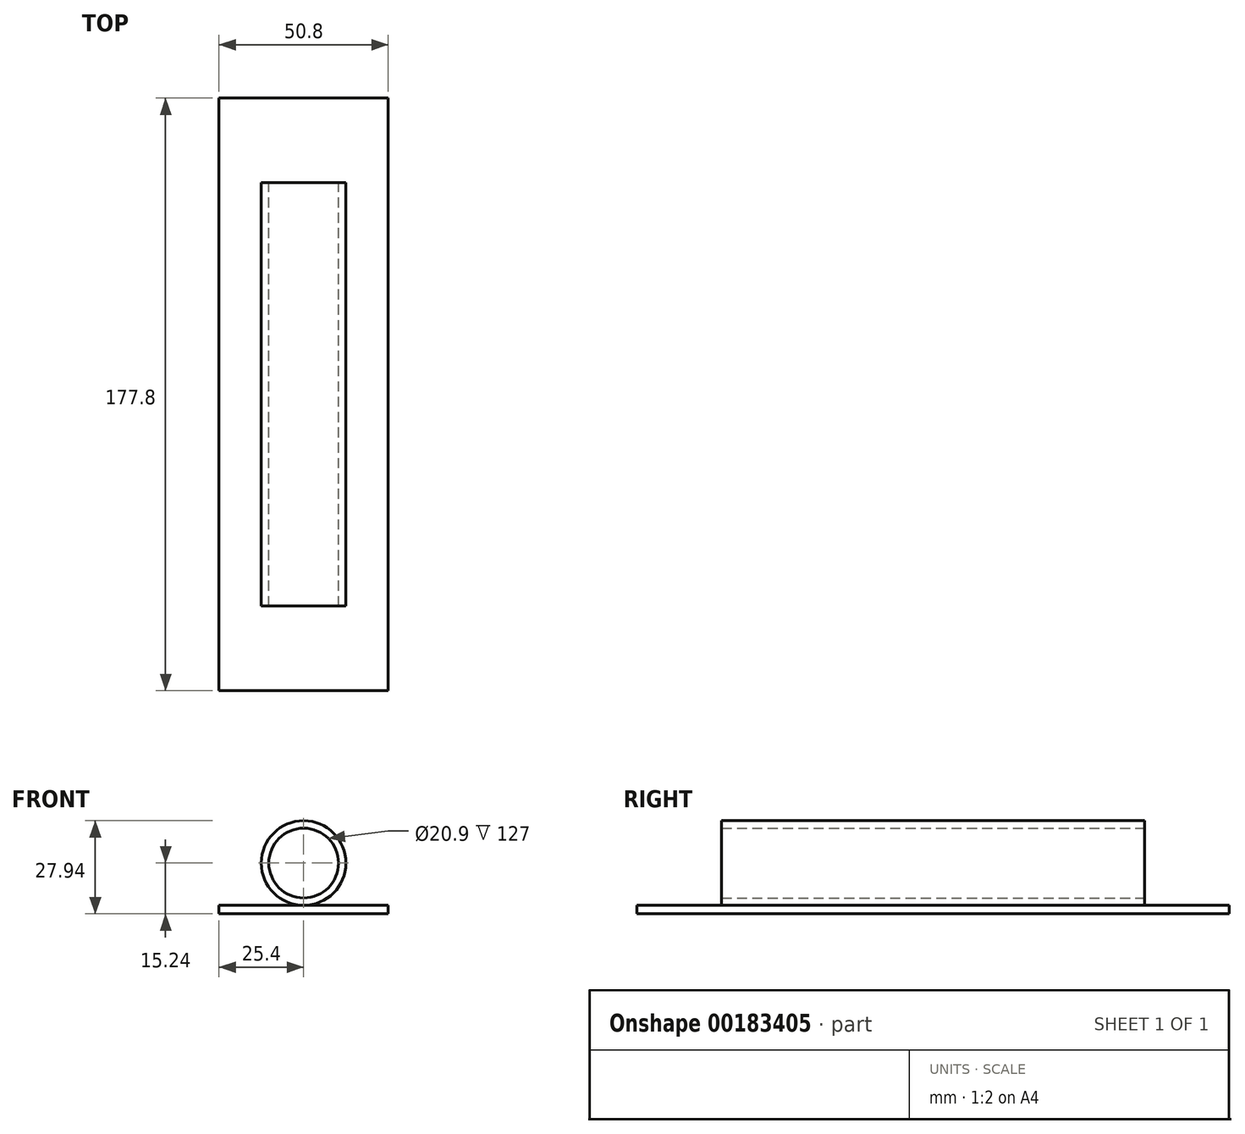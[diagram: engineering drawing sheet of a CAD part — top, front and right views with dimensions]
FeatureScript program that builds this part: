
annotation { "Feature Type Name" : "Feature", "Feature Type Description" : "" }
export const myFeature = defineFeature(function(context is Context, id is Id, definition is map)
    precondition{}
    {
        {
            var Q0;
            Q0=qCreatedBy(makeId("Front.planeOp"),FACE);
            var sketch = newSketch(context, id + "F0", { "sketchPlane" : qUnion([Q0])});
            skCircle(sketch, "E0", {"center": v(0, 0) * mm, "radius": 12.7 * mm});
            skCircle(sketch, "E1", {"center": v(0, 0) * mm, "radius": 10.45 * mm});
            skSolve(sketch);
        }
        {
            var Q0;
            Q0=makeQuery(id+"F0.imprint","IMPRINT",FACE,{"disambiguationData":[TD([[makeQuery(id+"F0.imprint","IMPRINT",EDGE,{"derivedFrom":sQuery(id+"F0.wireOp",EDGE,"E0")}),1.0]])]});
            var Q1;
            Q1=sQuery(id+"F0.wireOp",EDGE,"E0");
            var Q2;
            Q2=sQuery(id+"F0.wireOp",EDGE,"E1");
            extrude(context, id + "F1", {"entities" : qUnion([Q0]), "surfaceEntities" : qUnion([Q1, Q2]), "depth" : 127 * mm});
        }
        {
            var Q0;
            Q0=makeQuery(id+"F1.opExtrude","SWEPT_BODY",BODY,{"disambiguationData":[OSD([sQuery(id+"F0.wireOp",EDGE,"E0")])]});
            transform(context, id + "F2", {"entities" : qUnion([Q0]), "transformType" : TransformType.TRANSLATION_3D, "dx" : 0 * mm, "dy" : 0 * mm, "dz" : 12.7 * mm, "makeCopy" : false});
        }
        {
            var Q0;
            Q0=qCreatedBy(makeId("Top.planeOp"),FACE);
            var sketch = newSketch(context, id + "F3", { "sketchPlane" : qUnion([Q0])});
            skLineSegment(sketch, "E2.bottom", {"start": v(-25.4, 25.4) * mm, "end": v(25.4, 25.4) * mm});
            skLineSegment(sketch, "E2.top", {"start": v(-25.4, -152.4) * mm, "end": v(25.4, -152.4) * mm});
            skLineSegment(sketch, "E2.left", {"start": v(-25.4, 25.4) * mm, "end": v(-25.4, -152.4) * mm});
            skLineSegment(sketch, "E2.right", {"start": v(25.4, 25.4) * mm, "end": v(25.4, -152.4) * mm});
            skSolve(sketch);
        }
        {
            var Q0;
            Q0 = qSketchRegion(id + "F3", true);
            extrude(context, id + "F4", {"entities" : qUnion([Q0]), "oppositeDirection" : true, "depth" : 2.54 * mm});
        }
    });
